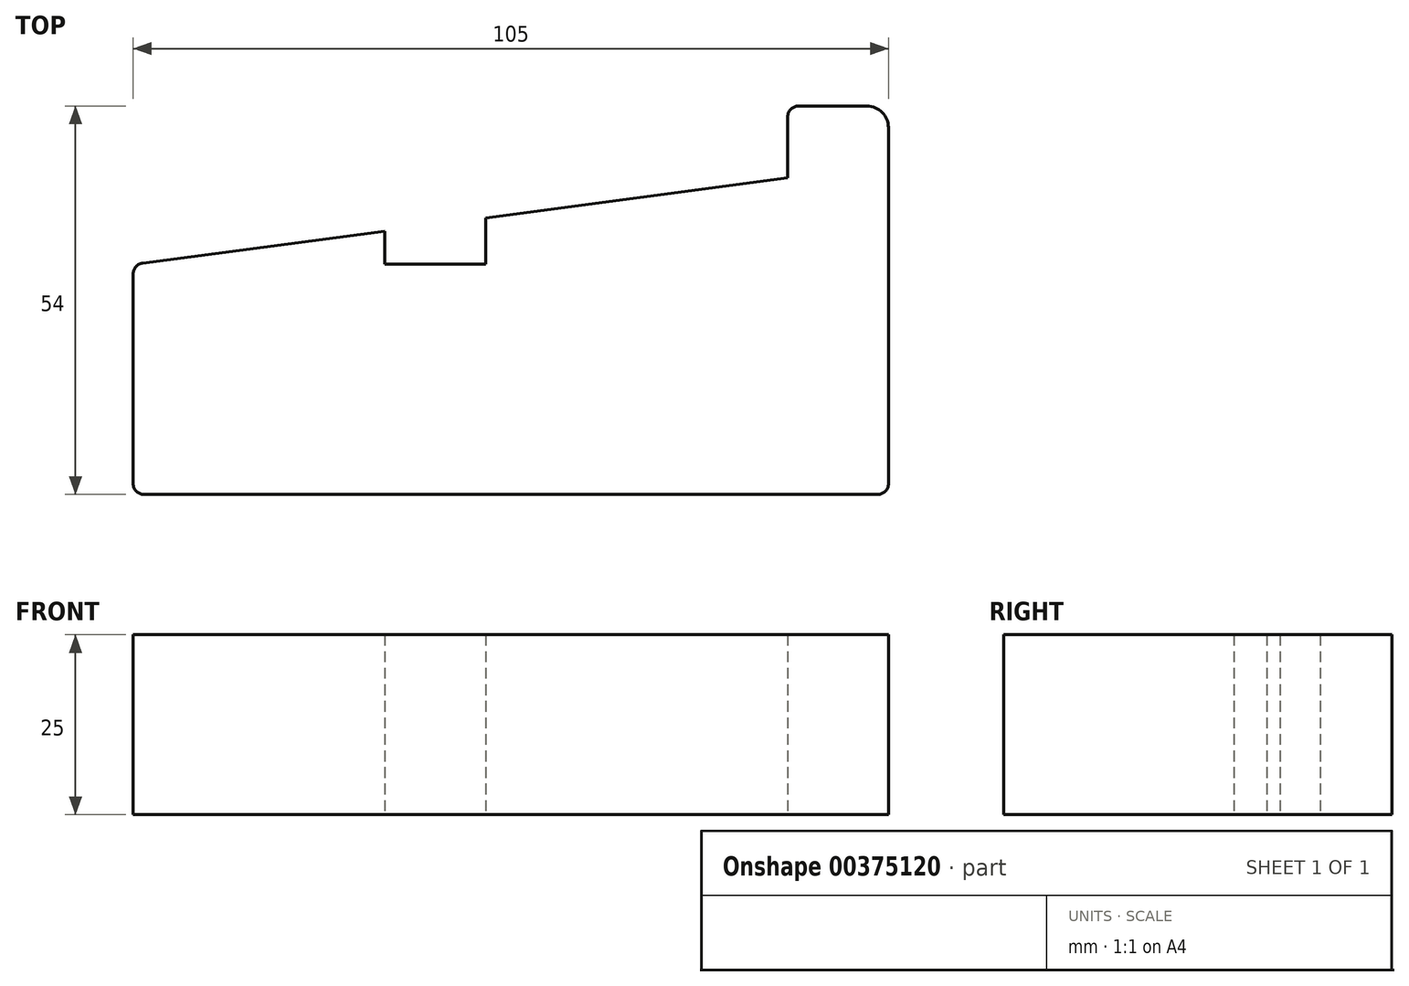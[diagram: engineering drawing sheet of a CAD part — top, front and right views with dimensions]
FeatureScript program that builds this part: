
annotation { "Feature Type Name" : "Feature", "Feature Type Description" : "" }
export const myFeature = defineFeature(function(context is Context, id is Id, definition is map)
    precondition{}
    {
        {
            var Q0;
            Q0=qCreatedBy(makeId("Top.planeOp"),FACE);
            var sketch = newSketch(context, id + "F0", { "sketchPlane" : qUnion([Q0])});
            skLineSegment(sketch, "E0", {"start": v(-105, -54.96) * mm, "end": v(-1.5, -54.96) * mm});
            skLineSegment(sketch, "E1", {"start": v(0, -53.46) * mm, "end": v(0, -3.96) * mm});
            skLineSegment(sketch, "E2", {"start": v(-3, -0.96) * mm, "end": v(-12.5, -0.96) * mm});
            skLineSegment(sketch, "E3", {"start": v(-105, -53.46) * mm, "end": v(-105, -24.27) * mm});
            skLineSegment(sketch, "E4", {"start": v(-103.5, -54.96) * mm, "end": v(-56, -54.96) * mm});
            skLineSegment(sketch, "E5", {"start": v(-14, -2.46) * mm, "end": v(-14, -10.96) * mm});
            skLineSegment(sketch, "E6", {"start": v(-14, -10.96) * mm, "end": v(-56, -16.5) * mm});
            skLineSegment(sketch, "E7", {"start": v(-56, -22.96) * mm, "end": v(-56, -16.5) * mm});
            skLineSegment(sketch, "E8", {"start": v(-56, -22.96) * mm, "end": v(-70, -22.96) * mm});
            skLineSegment(sketch, "E9", {"start": v(-70, -18.34) * mm, "end": v(-70, -22.96) * mm});
            skLineSegment(sketch, "E10.trimOffspring", {"start": v(-70, -18.34) * mm, "end": v(-103.7, -22.79) * mm});
            skPoint(sketch, "E11.visualSharp", {"position": v(-105, -22.96) * mm});
            skArc(sketch, "E11.filletArc", {"start": v(-103.7, -22.79) * mm, "mid": v(-104.63, -23.28) * mm, "end": v(-105, -24.27) * mm});
            skPoint(sketch, "E12.visualSharp", {"position": v(-105, -54.96) * mm});
            skArc(sketch, "E12.filletArc", {"start": v(-105, -53.46) * mm, "mid": v(-104.56, -54.52) * mm, "end": v(-103.5, -54.96) * mm});
            skPoint(sketch, "E13.visualSharp", {"position": v(0, -54.96) * mm});
            skArc(sketch, "E13.filletArc", {"start": v(-1.5, -54.96) * mm, "mid": v(-0.44, -54.52) * mm, "end": v(0, -53.46) * mm});
            skPoint(sketch, "E14.visualSharp", {"position": v(-14, -0.96) * mm});
            skArc(sketch, "E14.filletArc", {"start": v(-12.5, -0.96) * mm, "mid": v(-13.56, -1.4) * mm, "end": v(-14, -2.46) * mm});
            skPoint(sketch, "E15.visualSharp", {"position": v(0, -0.96) * mm});
            skArc(sketch, "E15.filletArc", {"start": v(0, -3.96) * mm, "mid": v(-0.88, -1.84) * mm, "end": v(-3, -0.96) * mm});
            skSolve(sketch);
        }
        {
            var Q0;
            Q0 = qSketchRegion(id + "F0", true);
            extrude(context, id + "F1", {"entities" : qUnion([Q0]), "depth" : 25 * mm});
        }
    });
